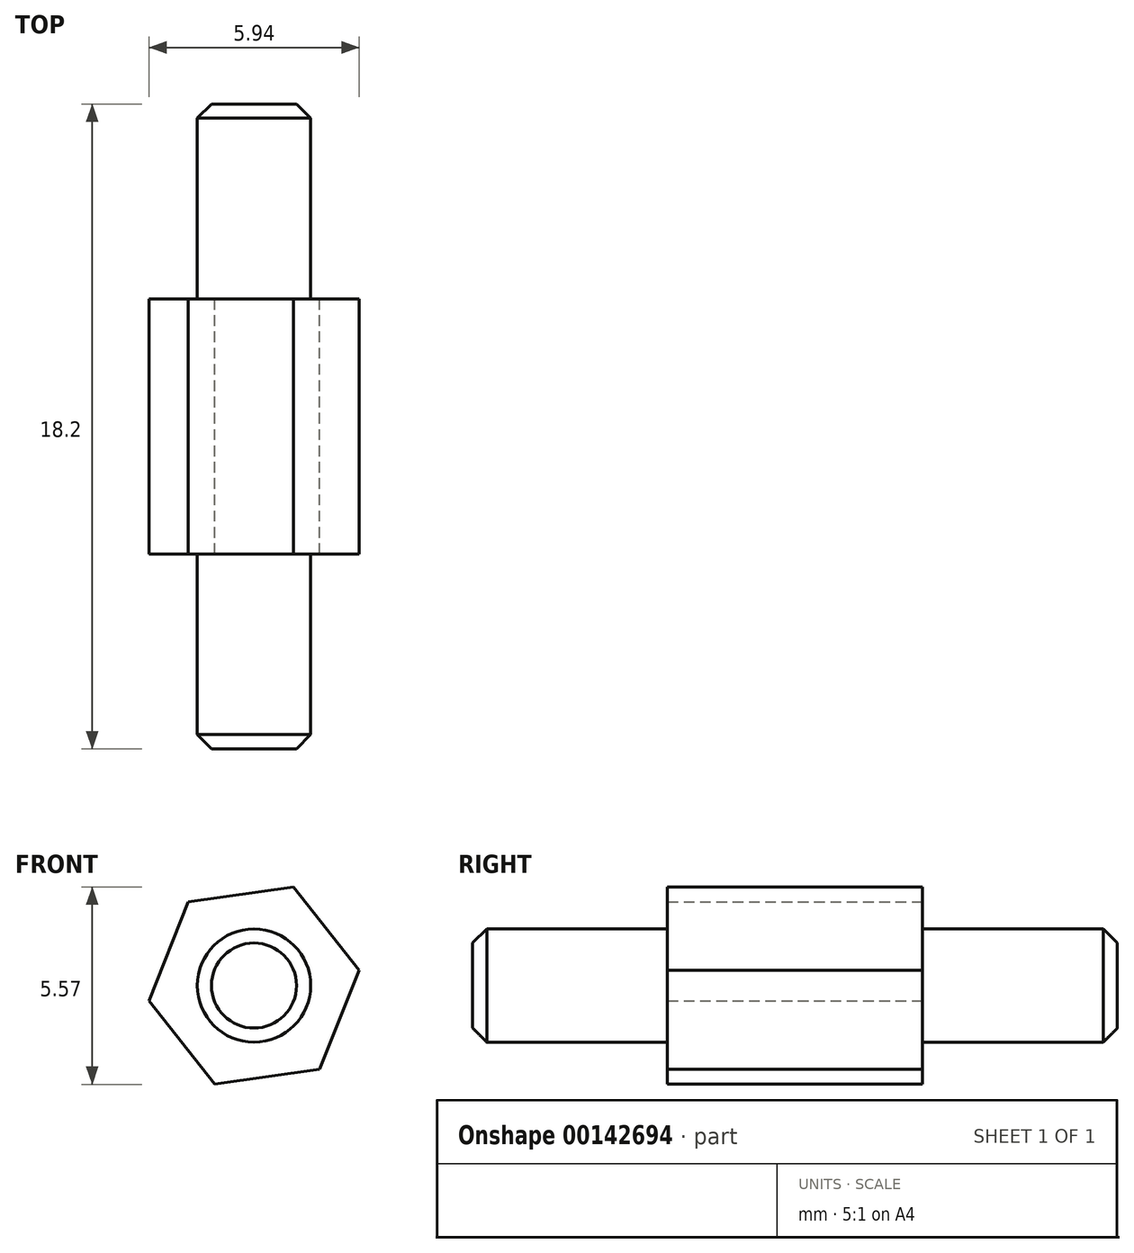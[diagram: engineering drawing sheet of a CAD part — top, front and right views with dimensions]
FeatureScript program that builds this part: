
annotation { "Feature Type Name" : "Feature", "Feature Type Description" : "" }
export const myFeature = defineFeature(function(context is Context, id is Id, definition is map)
    precondition{}
    {
        {
            var Q0;
            Q0=qCreatedBy(makeId("Front.planeOp"),FACE);
            var sketch = newSketch(context, id + "F0", { "sketchPlane" : qUnion([Q0])});
            skCircle(sketch, "E0", {"center": v(-38.08, 31.62) * mm, "radius": 1.6 * mm});
            skCircle(sketch, "E1.cCircle", {"center": v(-38.08, 31.62) * mm, "radius": 3 * mm, "construction": true});
            skLineSegment(sketch, "E1.0", {"start": v(-36.97, 34.4) * mm, "end": v(-35.11, 32.05) * mm});
            skLineSegment(sketch, "E1.1", {"start": v(-35.11, 32.05) * mm, "end": v(-36.23, 29.26) * mm});
            skLineSegment(sketch, "E1.2", {"start": v(-36.23, 29.26) * mm, "end": v(-39.2, 28.83) * mm});
            skLineSegment(sketch, "E1.3", {"start": v(-39.2, 28.83) * mm, "end": v(-41.05, 31.2) * mm});
            skLineSegment(sketch, "E1.4", {"start": v(-41.05, 31.2) * mm, "end": v(-39.94, 33.98) * mm});
            skLineSegment(sketch, "E1.5", {"start": v(-39.94, 33.98) * mm, "end": v(-36.97, 34.4) * mm});
            skSolve(sketch);
        }
        {
            var Q0;
            Q0=makeQuery(id+"F0.imprint","IMPRINT",FACE,{"disambiguationData":[TD([[makeQuery(id+"F0.imprint","IMPRINT",EDGE,{"derivedFrom":sQuery(id+"F0.wireOp",EDGE,"E0")}),-1.0]])]});
            var Q1;
            Q1=makeQuery(id+"F0.imprint","IMPRINT",FACE,{"disambiguationData":[TD([[makeQuery(id+"F0.imprint","IMPRINT",EDGE,{"derivedFrom":sQuery(id+"F0.wireOp",EDGE,"E0")}),1.0]])]});
            extrude(context, id + "F1", {"entities" : qUnion([Q0, Q1]), "depth" : 7.2 * mm});
        }
        {
            var Q0;
            Q0=makeQuery(id+"F0.imprint","IMPRINT",FACE,{"disambiguationData":[TD([[makeQuery(id+"F0.imprint","IMPRINT",EDGE,{"derivedFrom":sQuery(id+"F0.wireOp",EDGE,"E0")}),1.0]])]});
            extrude(context, id + "F2", {"entities" : qUnion([Q0]), "operationType" : NewBodyOperationType.ADD, "oppositeDirection" : true, "depth" : 5.5 * mm});
        }
        {
            var Q0;
            Q0=makeQuery(id+"F1.opExtrude","CAP_FACE",FACE,{"disambiguationData":[OSD([sQuery(id+"F0.wireOp",EDGE,"E1.0"),sQuery(id+"F0.wireOp",EDGE,"E1.1"),sQuery(id+"F0.wireOp",EDGE,"E1.2"),sQuery(id+"F0.wireOp",EDGE,"E1.3"),sQuery(id+"F0.wireOp",EDGE,"E1.4"),sQuery(id+"F0.wireOp",EDGE,"E1.5")])],"isStart":false});
            var sketch = newSketch(context, id + "F3", { "sketchPlane" : qUnion([Q0])});
            skCircle(sketch, "E2.0", {"center": v(-38.08, 31.62) * mm, "radius": 1.6 * mm});
            skSolve(sketch);
        }
        {
            var Q0;
            Q0=makeQuery(id+"F3.imprint","IMPRINT",FACE,{"disambiguationData":[TD([[makeQuery(id+"F3.imprint","IMPRINT",EDGE,{"derivedFrom":sQuery(id+"F3.wireOp",EDGE,"E2.0")}),1.0]])]});
            extrude(context, id + "F4", {"entities" : qUnion([Q0]), "operationType" : NewBodyOperationType.ADD, "depth" : 5.5 * mm});
        }
        {
            var Q0;
            Q0=makeQuery(id+"F2.opExtrude","CAP_EDGE",EDGE,{"disambiguationData":[OSD([sQuery(id+"F0.wireOp",EDGE,"E0")])],"isStart":false});
            var Q1;
            Q1=makeQuery(id+"F4.opExtrude","CAP_EDGE",EDGE,{"disambiguationData":[OSD([sQuery(id+"F3.wireOp",EDGE,"E2.0")])],"isStart":false});
            chamfer(context, id + "F5", {"entities" : qUnion([Q0, Q1]), "width" : .4 * mm, "tangentPropagation" : true});
        }
    });
